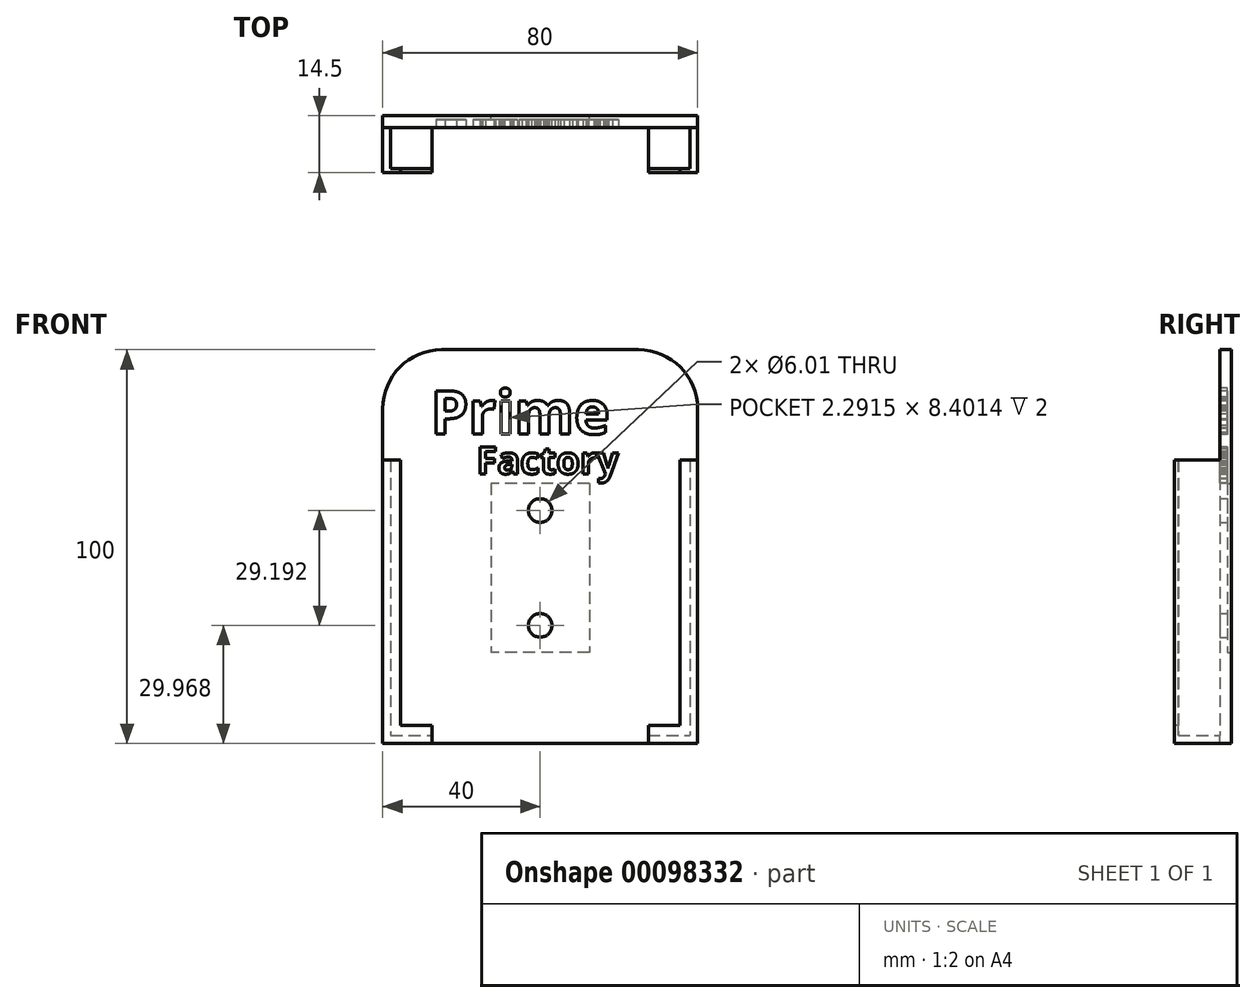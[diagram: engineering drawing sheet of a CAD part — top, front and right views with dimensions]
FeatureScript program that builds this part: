
annotation { "Feature Type Name" : "Feature", "Feature Type Description" : "" }
export const myFeature = defineFeature(function(context is Context, id is Id, definition is map)
    precondition{}
    {
        {
            var Q0;
            Q0=qCreatedBy(makeId("Front.planeOp"),FACE);
            var sketch = newSketch(context, id + "F0", { "sketchPlane" : qUnion([Q0])});
            skLineSegment(sketch, "E0.bottom", {"start": v(-38, 35) * mm, "end": v(38, 35) * mm});
            skLineSegment(sketch, "E0.top", {"start": v(-38, -35) * mm, "end": v(38, -35) * mm});
            skLineSegment(sketch, "E0.left", {"start": v(-38, 35) * mm, "end": v(-38, -35) * mm});
            skLineSegment(sketch, "E0.right", {"start": v(38, 35) * mm, "end": v(38, -35) * mm});
            skPoint(sketch, "E0.middle", {"position": v(0, 0) * mm});
            skLineSegment(sketch, "E1.top", {"start": v(-40, -37) * mm, "end": v(40, -37) * mm});
            skLineSegment(sketch, "E2", {"start": v(-38, 35) * mm, "end": v(-40, 35) * mm});
            skLineSegment(sketch, "E3", {"start": v(38, 35) * mm, "end": v(40, 35) * mm});
            skLineSegment(sketch, "E4", {"start": v(-40, 35) * mm, "end": v(-40, -37) * mm});
            skLineSegment(sketch, "E5", {"start": v(40, 35) * mm, "end": v(40, -37) * mm});
            skSolve(sketch);
        }
        {
            var Q0;
            Q0=makeQuery(id+"F0.imprint","IMPRINT",FACE,{"disambiguationData":[TD([[makeQuery(id+"F0.imprint","IMPRINT",EDGE,{"derivedFrom":sQuery(id+"F0.wireOp",EDGE,"E0.top")}),-1.0]])]});
            extrude(context, id + "F1", {"entities" : qUnion([Q0]), "depth" : 13 * mm});
        }
        {
            var Q0;
            Q0=makeQuery(id+"F1.opExtrude","CAP_FACE",FACE,{"disambiguationData":[OSD([sQuery(id+"F0.wireOp",EDGE,"E0.top"),sQuery(id+"F0.wireOp",EDGE,"E0.left"),sQuery(id+"F0.wireOp",EDGE,"E0.right"),sQuery(id+"F0.wireOp",EDGE,"E1.top"),sQuery(id+"F0.wireOp",EDGE,"E2"),sQuery(id+"F0.wireOp",EDGE,"E3"),sQuery(id+"F0.wireOp",EDGE,"E4"),sQuery(id+"F0.wireOp",EDGE,"E5")])],"isStart":true});
            var sketch = newSketch(context, id + "F2", { "sketchPlane" : qUnion([Q0])});
            skLineSegment(sketch, "E6.bottom", {"start": v(-40, -37) * mm, "end": v(40, -37) * mm});
            skLineSegment(sketch, "E6.top", {"start": v(-40, 63) * mm, "end": v(40, 63) * mm});
            skLineSegment(sketch, "E6.left", {"start": v(-40, -37) * mm, "end": v(-40, 63) * mm});
            skLineSegment(sketch, "E6.right", {"start": v(40, -37) * mm, "end": v(40, 63) * mm});
            skSolve(sketch);
        }
        {
            var Q0;
            {var subQ2=sQuery(id+"F2.wireOp",EDGE,"E6.top");Q0=makeQuery(id+"F2.imprint","IMPRINT",FACE,{"disambiguationData":[TD([[makeQuery(id+"F2.imprint","IMPRINT",EDGE,{"derivedFrom":subQ2}),-1.0]])]});}
            extrude(context, id + "F3", {"entities" : qUnion([Q0]), "operationType" : NewBodyOperationType.ADD, "oppositeDirection" : true, "depth" : 3 * mm});
        }
        {
            var Q0;
            Q0=makeQuery(id+"F1.opExtrude","CAP_FACE",FACE,{"disambiguationData":[OSD([sQuery(id+"F0.wireOp",EDGE,"E0.top"),sQuery(id+"F0.wireOp",EDGE,"E0.left"),sQuery(id+"F0.wireOp",EDGE,"E0.right"),sQuery(id+"F0.wireOp",EDGE,"E1.top"),sQuery(id+"F0.wireOp",EDGE,"E2"),sQuery(id+"F0.wireOp",EDGE,"E3"),sQuery(id+"F0.wireOp",EDGE,"E4"),sQuery(id+"F0.wireOp",EDGE,"E5")])],"isStart":false});
            var sketch = newSketch(context, id + "F4", { "sketchPlane" : qUnion([Q0])});
            skLineSegment(sketch, "E7.bottom", {"start": v(40, -37) * mm, "end": v(35.5, -37) * mm});
            skLineSegment(sketch, "E7.top", {"start": v(40, 35) * mm, "end": v(35.5, 35) * mm});
            skLineSegment(sketch, "E7.left", {"start": v(40, -37) * mm, "end": v(40, 35) * mm});
            skLineSegment(sketch, "E7.right", {"start": v(35.5, -37) * mm, "end": v(35.5, 35) * mm});
            skLineSegment(sketch, "E8.bottom", {"start": v(-40, -37) * mm, "end": v(-35.5, -37) * mm});
            skLineSegment(sketch, "E8.top", {"start": v(-40, 35) * mm, "end": v(-35.5, 35) * mm});
            skLineSegment(sketch, "E8.left", {"start": v(-40, -37) * mm, "end": v(-40, 35) * mm});
            skLineSegment(sketch, "E8.right", {"start": v(-35.5, -37) * mm, "end": v(-35.5, 35) * mm});
            skLineSegment(sketch, "E9.bottom", {"start": v(-35.5, -37) * mm, "end": v(35.5, -37) * mm});
            skLineSegment(sketch, "E9.top", {"start": v(-35.5, -32.5) * mm, "end": v(35.5, -32.5) * mm});
            skLineSegment(sketch, "E9.left", {"start": v(-35.5, -37) * mm, "end": v(-35.5, -32.5) * mm});
            skLineSegment(sketch, "E9.right", {"start": v(35.5, -37) * mm, "end": v(35.5, -32.5) * mm});
            skSolve(sketch);
        }
        {
            var Q0;
            Q0 = qSketchRegion(id + "F4", true);
            extrude(context, id + "F5", {"entities" : qUnion([Q0]), "operationType" : NewBodyOperationType.ADD, "depth" : 1 * mm});
        }
        {
            var Q0;
            Q0=makeQuery(id+"F3.opExtrude","SWEPT_EDGE",EDGE,{"disambiguationData":[OSD([sQuery(id+"F2.wireOp",EDGE,"E6.top"),sQuery(id+"F2.wireOp",EDGE,"E6.right")])]});
            var Q1;
            Q1=makeQuery(id+"F3.opExtrude","SWEPT_EDGE",EDGE,{"disambiguationData":[OSD([sQuery(id+"F2.wireOp",EDGE,"E6.top"),sQuery(id+"F2.wireOp",EDGE,"E6.left")])]});
            fillet(context, id + "F6", {"entities" : qUnion([Q0, Q1]), "radius" : 15 * mm, "tangentPropagation" : true, "allowEdgeOverflow" : false});
        }
        {
            var Q0;
            Q0=makeQuery(id+"F5.opExtrude","CAP_FACE",FACE,{"disambiguationData":[OSD([sQuery(id+"F4.wireOp",EDGE,"E7.bottom"),sQuery(id+"F4.wireOp",EDGE,"E7.top"),sQuery(id+"F4.wireOp",EDGE,"E7.left"),sQuery(id+"F4.wireOp",EDGE,"E7.right"),sQuery(id+"F4.wireOp",EDGE,"E8.bottom"),sQuery(id+"F4.wireOp",EDGE,"E8.top"),sQuery(id+"F4.wireOp",EDGE,"E8.left"),sQuery(id+"F4.wireOp",EDGE,"E8.right"),sQuery(id+"F4.wireOp",EDGE,"E9.bottom"),sQuery(id+"F4.wireOp",EDGE,"E9.top")])],"isStart":false});
            var sketch = newSketch(context, id + "F7", { "sketchPlane" : qUnion([Q0])});
            skPoint(sketch, "E10", {"position": v(0, -32.5) * mm});
            skPoint(sketch, "E11", {"position": v(0, -37) * mm});
            skLineSegment(sketch, "E12.bottom", {"start": v(-5.52, -37) * mm, "end": v(9.48, -37) * mm});
            skLineSegment(sketch, "E12.top", {"start": v(-5.52, -32.5) * mm, "end": v(9.48, -32.5) * mm});
            skLineSegment(sketch, "E12.left", {"start": v(-5.52, -37) * mm, "end": v(-5.52, -32.5) * mm});
            skLineSegment(sketch, "E12.right", {"start": v(9.48, -37) * mm, "end": v(9.48, -32.5) * mm});
            skPoint(sketch, "E12.middle", {"position": v(1.98, -34.75) * mm});
            skSolve(sketch);
        }
        {
            var Q0;
            Q0 = qSketchRegion(id + "F7", true);
            extrude(context, id + "F8", {"entities" : qUnion([Q0]), "operationType" : NewBodyOperationType.REMOVE, "oppositeDirection" : true, "depth" : 11 * mm});
        }
        {
            var Q0;
            Q0=makeQuery(id+"F8.boolean.opBoolean","MERGE",FACE,{"derivedFrom":[makeQuery(id+"F3.opExtrude","CAP_FACE",FACE,{"disambiguationData":[OSD([sQuery(id+"F0.wireOp",EDGE,"E0.top"),sQuery(id+"F0.wireOp",EDGE,"E0.left"),sQuery(id+"F0.wireOp",EDGE,"E0.right"),sQuery(id+"F0.wireOp",EDGE,"E2"),sQuery(id+"F0.wireOp",EDGE,"E3"),sQuery(id+"F2.wireOp",EDGE,"E6.top"),sQuery(id+"F2.wireOp",EDGE,"E6.left"),sQuery(id+"F2.wireOp",EDGE,"E6.right")])],"isStart":false}),makeQuery(id+"F8.opExtrude","CAP_FACE",FACE,{"disambiguationData":[OSD([sQuery(id+"F7.wireOp",EDGE,"E12.bottom"),sQuery(id+"F7.wireOp",EDGE,"E12.top"),sQuery(id+"F7.wireOp",EDGE,"E12.left"),sQuery(id+"F7.wireOp",EDGE,"E12.right")])],"isStart":false})]});
            var sketch = newSketch(context, id + "F9", { "sketchPlane" : qUnion([Q0])});
            skLineSegment(sketch, "E13.bottom", {"start": v(-5.52, -35) * mm, "end": v(9.48, -35) * mm});
            skLineSegment(sketch, "E13.top", {"start": v(-5.52, -37.37) * mm, "end": v(9.48, -37.37) * mm});
            skLineSegment(sketch, "E13.left", {"start": v(-5.52, -35) * mm, "end": v(-5.52, -37.37) * mm});
            skLineSegment(sketch, "E13.right", {"start": v(9.48, -35) * mm, "end": v(9.48, -37.37) * mm});
            skSolve(sketch);
        }
        {
            var Q0;
            {var subQ0=sQuery(id+"F0.wireOp",EDGE,"E3");var subQ1=sQuery(id+"F0.wireOp",EDGE,"E2");var subQ2=sQuery(id+"F0.wireOp",EDGE,"E0.right");var subQ3=sQuery(id+"F0.wireOp",EDGE,"E0.left");var subQ4=sQuery(id+"F0.wireOp",EDGE,"E0.top");Q0=makeQuery(id+"F3.boolean.opBoolean","MERGE",FACE,{"derivedFrom":[makeQuery(id+"F1.opExtrude","CAP_FACE",FACE,{"disambiguationData":[OSD([subQ4,subQ3,subQ2,sQuery(id+"F0.wireOp",EDGE,"E1.top"),subQ1,subQ0,sQuery(id+"F0.wireOp",EDGE,"E4"),sQuery(id+"F0.wireOp",EDGE,"E5")])],"isStart":true}),makeQuery(id+"F3.opExtrude","CAP_FACE",FACE,{"disambiguationData":[OSD([subQ4,subQ3,subQ2,subQ1,subQ0,sQuery(id+"F2.wireOp",EDGE,"E6.top"),sQuery(id+"F2.wireOp",EDGE,"E6.left"),sQuery(id+"F2.wireOp",EDGE,"E6.right")])],"isStart":true})]});}
            var sketch = newSketch(context, id + "F10", { "sketchPlane" : qUnion([Q0])});
            skPoint(sketch, "E14", {"position": v(0, 7.56) * mm});
            skLineSegment(sketch, "E15.bottom", {"start": v(-12, 29.06) * mm, "end": v(12, 29.06) * mm});
            skLineSegment(sketch, "E15.top", {"start": v(-12, -13.94) * mm, "end": v(12, -13.94) * mm});
            skLineSegment(sketch, "E15.left", {"start": v(-12, 29.06) * mm, "end": v(-12, -13.94) * mm});
            skLineSegment(sketch, "E15.right", {"start": v(12, 29.06) * mm, "end": v(12, -13.94) * mm});
            skSolve(sketch);
        }
        {
            var Q0;
            Q0=makeQuery(id+"F10.imprint","IMPRINT",FACE,{"disambiguationData":[TD([[makeQuery(id+"F10.imprint","IMPRINT",EDGE,{"derivedFrom":sQuery(id+"F10.wireOp",EDGE,"E15.bottom")}),-1.0]])]});
            extrude(context, id + "F11", {"entities" : qUnion([Q0]), "operationType" : NewBodyOperationType.REMOVE, "oppositeDirection" : true, "depth" : 1 * mm});
        }
        {
            var Q0;
            Q0=makeQuery(id+"F9.imprint","IMPRINT",FACE,{"disambiguationData":[TD([[makeQuery(id+"F9.imprint","IMPRINT",EDGE,{"derivedFrom":sQuery(id+"F9.wireOp",EDGE,"E13.bottom")}),1.0]])]});
            var sketch = newSketch(context, id + "F12", { "sketchPlane" : qUnion([Q0])});
            skSolve(sketch);
        }
        {
            var Q0;
            Q0=makeQuery(id+"F12.imprint","IMPRINT",FACE,{"disambiguationData":[TD([[makeQuery(id+"F12.imprint","IMPRINT",EDGE,{"derivedFrom":makeQuery(id+"F9.imprint","IMPRINT",EDGE,{"derivedFrom":sQuery(id+"F9.wireOp",EDGE,"E13.bottom")})}),1.0]])]});
            extrude(context, id + "F13", {"entities" : qUnion([Q0]), "operationType" : NewBodyOperationType.REMOVE, "depth" : 0.5 * mm});
        }
        {
            var Q0;
            Q0=makeQuery(id+"F8.boolean.opBoolean","COPY",FACE,{"derivedFrom":makeQuery(id+"F8.opExtrude","SWEPT_FACE",FACE,{"disambiguationData":[OSD([sQuery(id+"F7.wireOp",EDGE,"E12.left")])]})});
            extrude(context, id + "F14", {"entities" : qUnion([Q0]), "operationType" : NewBodyOperationType.REMOVE, "oppositeDirection" : true, "depth" : 30 * mm});
        }
        {
            var Q0;
            Q0=makeQuery(id+"F8.boolean.opBoolean","COPY",FACE,{"derivedFrom":makeQuery(id+"F8.opExtrude","SWEPT_FACE",FACE,{"disambiguationData":[OSD([sQuery(id+"F7.wireOp",EDGE,"E12.right")])]})});
            extrude(context, id + "F15", {"entities" : qUnion([Q0]), "operationType" : NewBodyOperationType.REMOVE, "oppositeDirection" : true, "depth" : 26 * mm});
        }
        {
            var Q0;
            Q0=makeQuery(id+"F15.boolean.opBoolean","COPY",FACE,{"derivedFrom":makeQuery(id+"F15.opExtrude","CAP_FACE",FACE,{"disambiguationData":[OSD([sQuery(id+"F7.wireOp",EDGE,"E12.right")])],"isStart":false})});
            extrude(context, id + "F16", {"entities" : qUnion([Q0]), "operationType" : NewBodyOperationType.ADD, "depth" : 8 * mm});
        }
        {
            var Q0;
            Q0=makeQuery(id+"F14.boolean.opBoolean","COPY",FACE,{"derivedFrom":makeQuery(id+"F14.opExtrude","CAP_FACE",FACE,{"disambiguationData":[OSD([sQuery(id+"F7.wireOp",EDGE,"E12.left")])],"isStart":false})});
            extrude(context, id + "F17", {"entities" : qUnion([Q0]), "operationType" : NewBodyOperationType.ADD, "depth" : 8 * mm});
        }
        {
            var Q0;
            Q0=makeQuery(id+"F9.imprint","IMPRINT",FACE,{"disambiguationData":[TD([[makeQuery(id+"F9.imprint","IMPRINT",EDGE,{"derivedFrom":sQuery(id+"F9.wireOp",EDGE,"E13.bottom")}),1.0]])]});
            var sketch = newSketch(context, id + "F18", { "sketchPlane" : qUnion([Q0])});
            skText(sketch, "E16", { "text": "Prime", "fontName": "OpenSans-Bold.ttf"});
            skText(sketch, "E17", { "text": "Factory", "fontName": "OpenSans-Bold.ttf"});
            const initialGuessF18  = {"E16": [-0.02786, 0.04156, 1, 0, 0.01108], "E17": [-0.01618, 0.03145, 1, 0, 0.00695]};
            skSetInitialGuess(sketch, initialGuessF18);
            skSolve(sketch);
        }
        {
            var Q0;
            Q0 = qSketchRegion(id + "F18", true);
            extrude(context, id + "F19", {"entities" : qUnion([Q0]), "operationType" : NewBodyOperationType.REMOVE, "oppositeDirection" : true, "depth" : 2 * mm});
        }
        {
            var Q0;
            Q0=makeQuery(id+"F11.boolean.opBoolean","COPY",FACE,{"derivedFrom":makeQuery(id+"F11.opExtrude","SWEPT_FACE",FACE,{"disambiguationData":[OSD([sQuery(id+"F10.wireOp",EDGE,"E15.left")])]})});
            extrude(context, id + "F20", {"entities" : qUnion([Q0]), "operationType" : NewBodyOperationType.REMOVE, "oppositeDirection" : true, "depth" : 0.5 * mm});
        }
        {
            var Q0;
            Q0=makeQuery(id+"F11.boolean.opBoolean","COPY",FACE,{"derivedFrom":makeQuery(id+"F11.opExtrude","SWEPT_FACE",FACE,{"disambiguationData":[OSD([sQuery(id+"F10.wireOp",EDGE,"E15.right")])]})});
            extrude(context, id + "F21", {"entities" : qUnion([Q0]), "operationType" : NewBodyOperationType.REMOVE, "oppositeDirection" : true, "depth" : 0.5 * mm});
        }
        {
            var Q0;
            {var subQ0=sQuery(id+"F7.wireOp",EDGE,"E12.left");var subQ1=sQuery(id+"F4.wireOp",EDGE,"E9.bottom");var subQ2=sQuery(id+"F4.wireOp",EDGE,"E8.bottom");var subQ3=sQuery(id+"F4.wireOp",EDGE,"E7.bottom");var subQ4=sQuery(id+"F4.wireOp",EDGE,"E8.top");var subQ5=sQuery(id+"F4.wireOp",EDGE,"E9.top");var subQ6=sQuery(id+"F4.wireOp",EDGE,"E8.left");var subQ7=sQuery(id+"F4.wireOp",EDGE,"E8.right");Q0=makeQuery(id+"F17.boolean.opBoolean","MERGE",FACE,{"derivedFrom":[makeQuery(id+"F8.boolean.opBoolean","SPLIT",FACE,{"disambiguationData":[TD([makeQuery(id+"F1.opExtrude","SWEPT_FACE",FACE,{"disambiguationData":[OSD([sQuery(id+"F0.wireOp",EDGE,"E2")])]})])],"derivedFrom":makeQuery(id+"F5.opExtrude","CAP_FACE",FACE,{"disambiguationData":[OSD([subQ3,sQuery(id+"F4.wireOp",EDGE,"E7.top"),sQuery(id+"F4.wireOp",EDGE,"E7.left"),sQuery(id+"F4.wireOp",EDGE,"E7.right"),subQ2,subQ4,subQ6,subQ7,subQ1,subQ5])],"isStart":false})}),makeQuery(id+"F17.opExtrude","SWEPT_FACE",FACE,{"disambiguationData":[OSD([subQ0]),TDD([makeQuery(id+"F14.boolean.opBoolean","COPY",EDGE,{"derivedFrom":makeQuery(id+"F14.opExtrude","CAP_EDGE",EDGE,{"disambiguationData":[OSD([subQ0]),TDD([makeQuery(id+"F8.boolean.opBoolean","COPY",EDGE,{"derivedFrom":makeQuery(id+"F8.opExtrude","CAP_EDGE",EDGE,{"disambiguationData":[OSD([subQ0])],"isStart":true})})])],"isStart":false})})])]})]});}
            var Q1;
            {var subQ0=sQuery(id+"F7.wireOp",EDGE,"E12.right");var subQ1=sQuery(id+"F4.wireOp",EDGE,"E7.left");var subQ2=sQuery(id+"F4.wireOp",EDGE,"E9.bottom");var subQ3=sQuery(id+"F4.wireOp",EDGE,"E8.bottom");var subQ4=sQuery(id+"F4.wireOp",EDGE,"E7.bottom");var subQ5=sQuery(id+"F4.wireOp",EDGE,"E7.right");var subQ6=sQuery(id+"F4.wireOp",EDGE,"E7.top");var subQ7=sQuery(id+"F4.wireOp",EDGE,"E9.top");Q1=makeQuery(id+"F16.boolean.opBoolean","MERGE",FACE,{"derivedFrom":[makeQuery(id+"F8.boolean.opBoolean","SPLIT",FACE,{"disambiguationData":[TD([makeQuery(id+"F1.opExtrude","SWEPT_FACE",FACE,{"disambiguationData":[OSD([sQuery(id+"F0.wireOp",EDGE,"E3")])]})])],"derivedFrom":makeQuery(id+"F5.opExtrude","CAP_FACE",FACE,{"disambiguationData":[OSD([subQ4,subQ6,subQ1,subQ5,subQ3,sQuery(id+"F4.wireOp",EDGE,"E8.top"),sQuery(id+"F4.wireOp",EDGE,"E8.left"),sQuery(id+"F4.wireOp",EDGE,"E8.right"),subQ2,subQ7])],"isStart":false})}),makeQuery(id+"F16.opExtrude","SWEPT_FACE",FACE,{"disambiguationData":[OSD([subQ0]),TDD([makeQuery(id+"F15.boolean.opBoolean","COPY",EDGE,{"derivedFrom":makeQuery(id+"F15.opExtrude","CAP_EDGE",EDGE,{"disambiguationData":[OSD([subQ0]),TDD([makeQuery(id+"F8.boolean.opBoolean","COPY",EDGE,{"derivedFrom":makeQuery(id+"F8.opExtrude","CAP_EDGE",EDGE,{"disambiguationData":[OSD([subQ0])],"isStart":true})})])],"isStart":false})})])]})]});}
            extrude(context, id + "F22", {"entities" : qUnion([Q0, Q1]), "operationType" : NewBodyOperationType.ADD, "depth" : 0.5 * mm});
        }
        {
            var Q0;
            {var subQ0=sQuery(id+"F7.wireOp",EDGE,"E12.left");var subQ1=sQuery(id+"F4.wireOp",EDGE,"E9.top");var subQ2=sQuery(id+"F4.wireOp",EDGE,"E9.bottom");var subQ3=sQuery(id+"F4.wireOp",EDGE,"E8.right");var subQ4=sQuery(id+"F4.wireOp",EDGE,"E8.left");var subQ5=sQuery(id+"F4.wireOp",EDGE,"E8.top");var subQ6=sQuery(id+"F4.wireOp",EDGE,"E8.bottom");var subQ7=sQuery(id+"F4.wireOp",EDGE,"E7.right");var subQ8=sQuery(id+"F4.wireOp",EDGE,"E7.left");var subQ9=sQuery(id+"F4.wireOp",EDGE,"E7.top");var subQ10=sQuery(id+"F4.wireOp",EDGE,"E7.bottom");Q0=makeQuery(id+"F17.boolean.opBoolean","MERGE",FACE,{"derivedFrom":[makeQuery(id+"F8.boolean.opBoolean","SPLIT",FACE,{"disambiguationData":[TD([makeQuery(id+"F1.opExtrude","SWEPT_FACE",FACE,{"disambiguationData":[OSD([sQuery(id+"F0.wireOp",EDGE,"E0.left")])]})])],"derivedFrom":makeQuery(id+"F5.opExtrude","CAP_FACE",FACE,{"disambiguationData":[OSD([subQ10,subQ9,subQ8,subQ7,subQ6,subQ5,subQ4,subQ3,subQ2,subQ1])],"isStart":true})}),makeQuery(id+"F17.opExtrude","SWEPT_FACE",FACE,{"disambiguationData":[OSD([subQ10,subQ9,subQ8,subQ7,subQ6,subQ5,subQ4,subQ3,subQ2,subQ1,subQ0])]})]});}
            var Q1;
            {var subQ0=sQuery(id+"F7.wireOp",EDGE,"E12.right");var subQ1=sQuery(id+"F4.wireOp",EDGE,"E9.top");var subQ2=sQuery(id+"F4.wireOp",EDGE,"E9.bottom");var subQ3=sQuery(id+"F4.wireOp",EDGE,"E8.right");var subQ4=sQuery(id+"F4.wireOp",EDGE,"E8.left");var subQ5=sQuery(id+"F4.wireOp",EDGE,"E8.top");var subQ6=sQuery(id+"F4.wireOp",EDGE,"E8.bottom");var subQ7=sQuery(id+"F4.wireOp",EDGE,"E7.right");var subQ8=sQuery(id+"F4.wireOp",EDGE,"E7.left");var subQ9=sQuery(id+"F4.wireOp",EDGE,"E7.top");var subQ10=sQuery(id+"F4.wireOp",EDGE,"E7.bottom");Q1=makeQuery(id+"F16.boolean.opBoolean","MERGE",FACE,{"derivedFrom":[makeQuery(id+"F8.boolean.opBoolean","SPLIT",FACE,{"disambiguationData":[TD([makeQuery(id+"F1.opExtrude","SWEPT_FACE",FACE,{"disambiguationData":[OSD([sQuery(id+"F0.wireOp",EDGE,"E0.right")])]})])],"derivedFrom":makeQuery(id+"F5.opExtrude","CAP_FACE",FACE,{"disambiguationData":[OSD([subQ10,subQ9,subQ8,subQ7,subQ6,subQ5,subQ4,subQ3,subQ2,subQ1])],"isStart":true})}),makeQuery(id+"F16.opExtrude","SWEPT_FACE",FACE,{"disambiguationData":[OSD([subQ10,subQ9,subQ8,subQ7,subQ6,subQ5,subQ4,subQ3,subQ2,subQ1,subQ0])]})]});}
            extrude(context, id + "F23", {"entities" : qUnion([Q0, Q1]), "operationType" : NewBodyOperationType.REMOVE, "oppositeDirection" : true, "depth" : 0.5 * mm});
        }
        {
            var Q0;
            {var subQ0=sQuery(id+"F10.wireOp",EDGE,"E15.right");var subQ1=sQuery(id+"F10.wireOp",EDGE,"E15.left");Q0=makeQuery(id+"F21.boolean.opBoolean","MERGE",FACE,{"derivedFrom":[makeQuery(id+"F20.boolean.opBoolean","MERGE",FACE,{"derivedFrom":[makeQuery(id+"F11.boolean.opBoolean","COPY",FACE,{"derivedFrom":makeQuery(id+"F11.opExtrude","CAP_FACE",FACE,{"disambiguationData":[OSD([sQuery(id+"F10.wireOp",EDGE,"E15.bottom"),sQuery(id+"F10.wireOp",EDGE,"E15.top"),subQ1,subQ0])],"isStart":false})}),makeQuery(id+"F20.opExtrude","SWEPT_FACE",FACE,{"disambiguationData":[OSD([subQ1]),TDD([makeQuery(id+"F11.boolean.opBoolean","COPY",EDGE,{"derivedFrom":makeQuery(id+"F11.opExtrude","CAP_EDGE",EDGE,{"disambiguationData":[OSD([subQ1])],"isStart":false})})])]})]}),makeQuery(id+"F21.opExtrude","SWEPT_FACE",FACE,{"disambiguationData":[OSD([subQ0]),TDD([makeQuery(id+"F11.boolean.opBoolean","COPY",EDGE,{"derivedFrom":makeQuery(id+"F11.opExtrude","CAP_EDGE",EDGE,{"disambiguationData":[OSD([subQ0])],"isStart":false})})])]})]});}
            var sketch = newSketch(context, id + "F24", { "sketchPlane" : qUnion([Q0])});
            skLineSegment(sketch, "E18.bottom", {"start": v(-12.5, 29.06) * mm, "end": v(12.5, 29.06) * mm});
            skLineSegment(sketch, "E18.top", {"start": v(-12.5, -13.94) * mm, "end": v(12.5, -13.94) * mm});
            skLineSegment(sketch, "E18.left", {"start": v(-12.5, 29.06) * mm, "end": v(-12.5, -13.94) * mm});
            skLineSegment(sketch, "E18.right", {"start": v(12.5, 29.06) * mm, "end": v(12.5, -13.94) * mm});
            skSolve(sketch);
        }
        {
            var Q0;
            {var subQ0=sQuery(id+"F4.wireOp",EDGE,"E7.left");Q0=makeQuery(id+"F22.boolean.opBoolean","MERGE",FACE,{"derivedFrom":[makeQuery(id+"F5.boolean.opBoolean","MERGE",FACE,{"derivedFrom":[makeQuery(id+"F3.boolean.opBoolean","MERGE",FACE,{"derivedFrom":[makeQuery(id+"F1.opExtrude","SWEPT_FACE",FACE,{"disambiguationData":[OSD([sQuery(id+"F0.wireOp",EDGE,"E5")])]}),makeQuery(id+"F3.opExtrude","SWEPT_FACE",FACE,{"disambiguationData":[OSD([sQuery(id+"F2.wireOp",EDGE,"E6.left")])]})]}),makeQuery(id+"F5.opExtrude","SWEPT_FACE",FACE,{"disambiguationData":[OSD([subQ0])]})]}),makeQuery(id+"F22.opExtrude","SWEPT_FACE",FACE,{"disambiguationData":[OSD([subQ0])]})]});}
            var sketch = newSketch(context, id + "F25", { "sketchPlane" : qUnion([Q0])});
            skSolve(sketch);
        }
        {
            var Q0;
            Q0=makeQuery(id+"F24.imprint","IMPRINT",FACE,{"disambiguationData":[TD([[makeQuery(id+"F24.imprint","IMPRINT",EDGE,{"derivedFrom":sQuery(id+"F24.wireOp",EDGE,"E18.bottom")}),-1.0]])]});
            var sketch = newSketch(context, id + "F26", { "sketchPlane" : qUnion([Q0])});
            skLineSegment(sketch, "E19", {"start": v(0, 29.06) * mm, "end": v(0, 22.16) * mm});
            skLineSegment(sketch, "E20", {"start": v(0, -13.94) * mm, "end": v(0, -7.03) * mm});
            skCircle(sketch, "E21", {"center": v(0, 22.16) * mm, "radius": 3 * mm});
            skCircle(sketch, "E22", {"center": v(0, -7.03) * mm, "radius": 3 * mm});
            skSolve(sketch);
        }
        {
            var Q0;
            Q0 = qSketchRegion(id + "F26", true);
            extrude(context, id + "F27", {"entities" : qUnion([Q0]), "operationType" : NewBodyOperationType.REMOVE, "oppositeDirection" : true, "depth" : 25 * mm});
        }
        {
            var Q0;
            Q0 = qSketchRegion(id + "F25", true);
            var Q1;
            Q1 = qSketchRegion(id + "F26", true);
            extrude(context, id + "F28", {"entities" : qUnion([Q0, Q1]), "operationType" : NewBodyOperationType.REMOVE, "oppositeDirection" : true, "depth" : 25 * mm});
        }
    });
